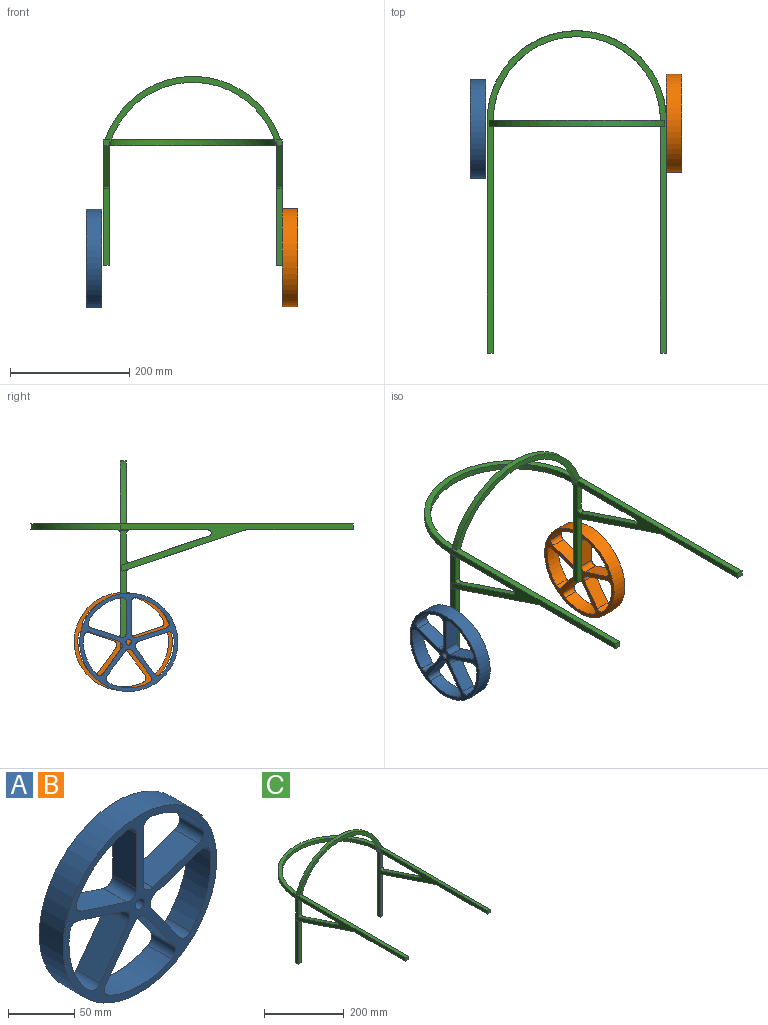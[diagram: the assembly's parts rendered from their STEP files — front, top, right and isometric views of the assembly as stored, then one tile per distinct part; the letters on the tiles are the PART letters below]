
ASSEMBLY  parts=3 mates=1
PART A: 34 faces, bbox 164.5x25.4x164.5 mm
  f0: cylinder r=75.96mm len=54.56mm, axis (0,1,0), area 1774.4mm2, adj f6,f7,f19,f20
  f1: cylinder r=75.96mm len=64.18mm, axis (0,1,0), area 1776.2mm2, adj f6,f7,f23,f24
  f2: cylinder r=75.96mm len=67.49mm, axis (0,1,0), area 1776.2mm2, adj f6,f7,f25,f26
  f3: cylinder r=75.96mm len=64.25mm, axis (0,1,0), area 1777.9mm2, adj f6,f7,f27,f28
  f4: cylinder r=75.96mm len=54.6mm, axis (0,1,0), area 1776.2mm2, adj f6,f7,f21,f22
  f5: cylinder r=82.23mm len=164.47mm, axis (0,1,0), area 13123.9mm2, adj f6,f7
  f6: plane 164.47x164.47mm, normal (0,-1,0), area 6130.5mm2, adj f0,f1,f2,f3,f4,f5,f8,f9
  f7: plane 164.47x164.47mm, normal (0,1,0), area 6130.5mm2, adj f0,f1,f2,f3,f4,f5,f8,f9
  f8: plane 49.09x25.4mm, normal (-0.31,0,0.95), area 1311.5mm2, adj f6,f7,f19,f29
  f9: plane 51.63x25.4mm, normal (1,0,0), area 1311.5mm2, adj f6,f7,f20,f29
  f10: plane 51.65x25.4mm, normal (-1,0,0), area 1311.8mm2, adj f6,f7,f21,f30
  f11: plane 49.12x25.4mm, normal (0.31,0,0.95), area 1311.8mm2, adj f6,f7,f22,f30
  f12: plane 49.12x25.4mm, normal (-0.31,0,-0.95), area 1311.8mm2, adj f6,f7,f23,f33
  f13: plane 41.78x30.36mm, normal (-0.81,0,0.59), area 1311.8mm2, adj f6,f7,f24,f33
  f14: plane 41.78x30.36mm, normal (0.81,0,-0.59), area 1311.8mm2, adj f6,f7,f25,f32
  f15: plane 41.78x30.36mm, normal (-0.81,0,-0.59), area 1311.8mm2, adj f6,f7,f26,f32
  f16: plane 41.8x30.37mm, normal (0.81,0,0.59), area 1312.2mm2, adj f6,f7,f27,f31
  f17: plane 49.12x25.4mm, normal (0.31,0,-0.95), area 1312.2mm2, adj f6,f7,f28,f31
  f18: cylinder r=4.79mm len=25.4mm, axis (0,1,0), area 764.3mm2, adj f6,f7
  f19: cylinder r=7.62mm len=25.4mm, axis (0,1,0), area 336.5mm2, adj f0,f6,f7,f8
  f20: cylinder r=7.62mm len=25.4mm, axis (0,1,0), area 336.5mm2, adj f0,f6,f7,f9
  f21: cylinder r=7.62mm len=25.4mm, axis (0,1,0), area 336.5mm2, adj f4,f6,f7,f10
  f22: cylinder r=7.62mm len=25.4mm, axis (0,1,0), area 336.5mm2, adj f4,f6,f7,f11
  f23: cylinder r=7.62mm len=25.4mm, axis (0,1,0), area 336.5mm2, adj f1,f6,f7,f12
  f24: cylinder r=7.62mm len=25.4mm, axis (0,1,0), area 336.5mm2, adj f1,f6,f7,f13
  f25: cylinder r=7.62mm len=25.4mm, axis (0,1,0), area 336.5mm2, adj f2,f6,f7,f14
  f26: cylinder r=7.62mm len=25.4mm, axis (0,1,0), area 336.5mm2, adj f2,f6,f7,f15
  f27: cylinder r=7.62mm len=25.4mm, axis (0,1,0), area 336.5mm2, adj f3,f6,f7,f16
  f28: cylinder r=7.62mm len=25.4mm, axis (0,1,0), area 336.5mm2, adj f3,f6,f7,f17
  f29: cylinder r=7.62mm len=25.4mm, axis (0,-1,0), area 365mm2, adj f6,f7,f8,f9
  f30: cylinder r=7.62mm len=25.4mm, axis (0,-1,0), area 364.8mm2, adj f6,f7,f10,f11
  f31: cylinder r=7.62mm len=25.4mm, axis (0,1,0), area 364.7mm2, adj f6,f7,f16,f17
  f32: cylinder r=7.62mm len=25.4mm, axis (0,1,0), area 364.8mm2, adj f6,f7,f14,f15
  f33: cylinder r=7.62mm len=25.4mm, axis (0,1,0), area 364.8mm2, adj f6,f7,f12,f13
PART B: same geometry as A
PART C: 51 faces, bbox 300x540x316.5 mm
  f0: cylinder r=150mm len=300mm, axis (0,0,1), area 5918.2mm2, adj f1,f3,f7,f9,f10,f11,f16,f17
  f1: plane 146.93x10mm, normal (0,0,-1), area 1321.7mm2, adj f0,f2,f17,f28,f34,f49,f50
  f2: plane 390x210mm, normal (1,0,0), area 7876.7mm2, adj f1,f3,f4,f6,f7,f8,f13,f18
  f3: plane 148.56x49.87mm, normal (0,0.32,0.95), area 1396.3mm2, adj f0,f2,f17,f34,f36
  f4: plane 205.49x68.98mm, normal (0,-0.32,-0.95), area 2061.9mm2, adj f2,f5,f17,f33,f35,f37
  f5: cylinder r=150mm len=140.24mm, axis (0,0,1), area 1333.9mm2, adj f4,f8,f20,f21,f33,f37
  f6: plane 179.71x10mm, normal (0,0,-1), area 1797.1mm2, adj f2,f17,f18,f35
  f7: plane 44.26x9.67mm, normal (0,-1,0), area 427.8mm2, adj f0,f2,f28,f36
  f8: plane 129.4x9.67mm, normal (0,-1,0), area 1250.8mm2, adj f2,f5,f21,f37
  f9: plane 146.93x10mm, normal (0,0,-1), area 1322.4mm2, adj f0,f14,f16,f26,f38
  f10: plane 44.26x9.67mm, normal (0,-1,0), area 427.8mm2, adj f0,f14,f26,f39
  f11: plane 299.83x144.92mm, normal (0,0,-1), area 4453.7mm2, adj f0,f13,f27,f29
  f12: plane 179.71x10mm, normal (0,0,-1), area 1797.1mm2, adj f14,f15,f16,f40
  f13: cylinder r=140mm len=280mm, axis (0,0,-1), area 4409.3mm2, adj f2,f11,f14,f19,f27,f29,f44
  f14: plane 390x210mm, normal (-1,0,0), area 7879.3mm2, adj f9,f10,f12,f13,f15,f19,f22,f23
  f15: plane 10x10mm, normal (0,-1,0), area 100mm2, adj f12,f14,f16,f19
  f16: plane 390x79.24mm, normal (1,0,0), area 6048.6mm2, adj f0,f9,f12,f15,f19,f30,f31,f32
  f17: plane 390x79.24mm, normal (-1,0,0), area 6048.6mm2, adj f0,f1,f3,f4,f6,f18,f19,f33
  f18: plane 10x10mm, normal (0,-1,0), area 100mm2, adj f2,f6,f17,f19
  f19: plane 540x300mm, normal (0,0,1), area 12214.9mm2, adj f0,f2,f13,f14,f15,f16,f17,f18
  f20: plane 194.92x10mm, normal (0,1,0), area 1949.2mm2, adj f0,f2,f5,f21,f29
  f21: plane 10x10mm, normal (0,0,-1), area 98.9mm2, adj f2,f5,f8,f20
  f22: plane 194.92x10mm, normal (0,1,0), area 1949.2mm2, adj f0,f14,f24,f25,f27
  f23: plane 129.4x9.67mm, normal (0,-1,0), area 1250.8mm2, adj f14,f24,f25,f41
  f24: cylinder r=150mm len=140.24mm, axis (0,0,1), area 1333.9mm2, adj f22,f23,f25,f31,f32,f41
  f25: plane 10x10mm, normal (0,0,-1), area 98.9mm2, adj f14,f22,f23,f24
  f26: cylinder r=5.08mm len=9.67mm, axis (1,0,0), area 76mm2, adj f0,f9,f10,f14
  f27: cylinder r=5.08mm len=10.09mm, axis (-1,0,0), area 79.8mm2, adj f0,f11,f13,f22
  f28: cylinder r=5.08mm len=9.67mm, axis (1,0,0), area 76mm2, adj f0,f1,f2,f7
  f29: cylinder r=5.08mm len=10.09mm, axis (-1,0,0), area 79.8mm2, adj f0,f11,f13,f20
  f30: plane 148.56x49.87mm, normal (0,0.32,0.95), area 1396.3mm2, adj f0,f14,f16,f38,f39
  f31: plane 205.49x68.98mm, normal (0,-0.32,-0.95), area 2061.9mm2, adj f14,f16,f24,f32,f40,f41
  f32: plane 9.48x3.18mm, normal (0,0.95,-0.32), area 0.1mm2, adj f16,f24,f31
  f33: plane 9.48x3.18mm, normal (0,0.95,-0.32), area 0.1mm2, adj f4,f5,f17
  f34: cylinder r=5.08mm len=10mm, axis (1,0,0), area 143.1mm2, adj f1,f2,f3,f17
  f35: cylinder r=5.08mm len=10mm, axis (-1,0,0), area 16.5mm2, adj f2,f4,f6,f17
  f36: cylinder r=5.08mm len=9.67mm, axis (-1,0,0), area 91.1mm2, adj f0,f2,f3,f7
  f37: cylinder r=5.08mm len=9.67mm, axis (1,0,0), area 60.7mm2, adj f2,f4,f5,f8
  f38: cylinder r=5.08mm len=10mm, axis (-1,0,0), area 143.1mm2, adj f9,f14,f16,f30
  f39: cylinder r=5.08mm len=9.67mm, axis (1,0,0), area 91.1mm2, adj f0,f10,f14,f30
  f40: cylinder r=5.08mm len=10mm, axis (1,0,0), area 16.5mm2, adj f12,f14,f16,f31
  f41: cylinder r=5.08mm len=9.67mm, axis (-1,0,0), area 60.7mm2, adj f14,f23,f24,f31
  f42: cylinder r=144.74mm len=279.25mm, axis (0,1,0), area 3775.4mm2, adj f43,f44,f46,f47
  f43: plane 294.04x116.74mm, normal (0,-1,0), area 3759.7mm2, adj f2,f14,f19,f42,f45,f46,f47
  f44: plane 294.04x116.74mm, normal (0,1,0), area 3759.7mm2, adj f13,f19,f42,f45,f46,f47
  f45: cylinder r=154.74mm len=294.04mm, axis (0,1,0), area 3879.7mm2, adj f19,f43,f44
  f46: plane 10x0.41mm, normal (0,0,-1), area 4.1mm2, adj f14,f42,f43,f44
  f47: plane 10x0.34mm, normal (0,0,-1), area 3.4mm2, adj f2,f42,f43,f44
  f48: plane 10x0.33mm, normal (0,0,-1), area 1.1mm2, adj f0,f49,f50
  f49: cylinder r=154.74mm len=10mm, axis (0,1,0), area 1.9mm2, adj f0,f1,f48,f50
  f50: plane 0.33x0.26mm, normal (0,-1,0), area 0.1mm2, adj f0,f1,f48,f49
PLACE A rot(axis=(0,0,1),90deg) t=(-172.12,90.61,-202.52)mm
PLACE B rot(axis=(0,0,1),90deg) t=(156.05,99.87,-201.3)mm
PLACE C t=(6.05,104.71,-14.35)mm
MATE planar B.f18 <-> C.f16  axis (-1,0,0) through (156.05,99.87,-201.3)mm
